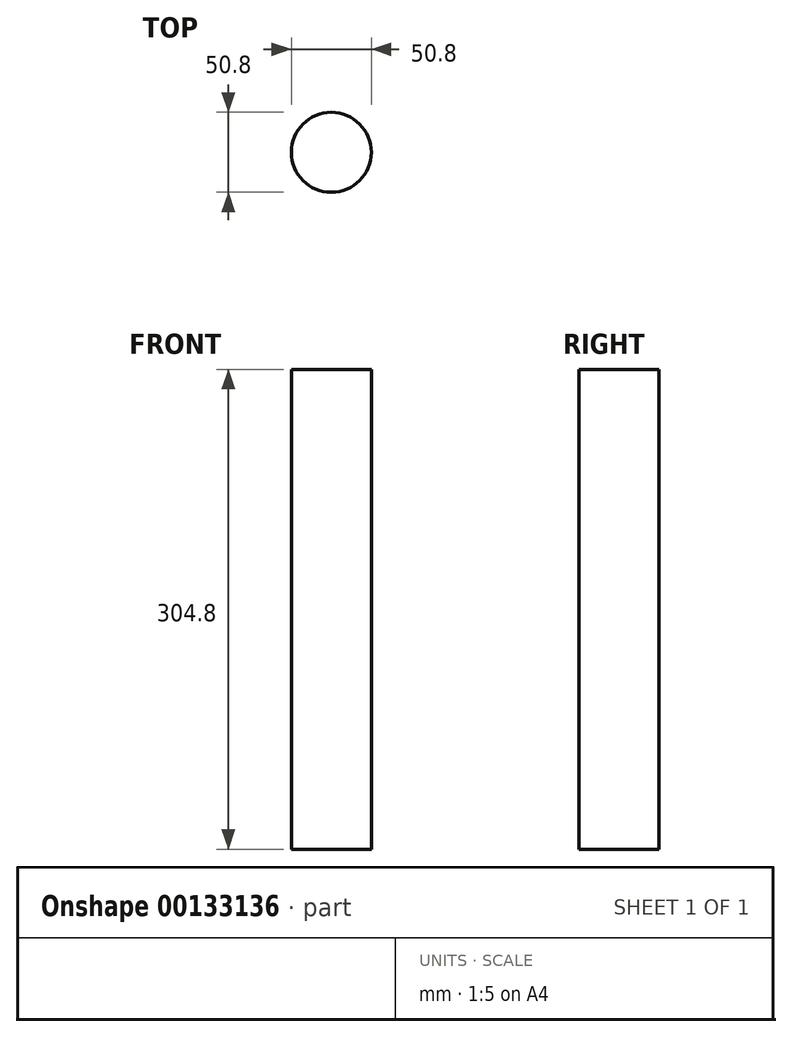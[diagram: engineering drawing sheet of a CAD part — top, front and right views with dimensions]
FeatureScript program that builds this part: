
annotation { "Feature Type Name" : "Feature", "Feature Type Description" : "" }
export const myFeature = defineFeature(function(context is Context, id is Id, definition is map)
    precondition{}
    {
        {
            var Q0;
            Q0=qCreatedBy(makeId("Top.planeOp"),FACE);
            var sketch = newSketch(context, id + "F0", { "sketchPlane" : qUnion([Q0])});
            skCircle(sketch, "E0", {"center": v(0, 0) * mm, "radius": 25.4 * mm});
            skSolve(sketch);
        }
        {
            var Q0;
            Q0 = qSketchRegion(id + "F0", true);
            extrude(context, id + "F1", {"entities" : qUnion([Q0]), "depth" : 304.8 * mm});
        }
    });
